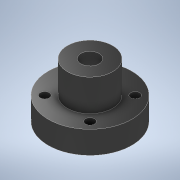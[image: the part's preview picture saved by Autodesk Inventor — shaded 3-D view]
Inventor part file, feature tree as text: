
AUTODESK INVENTOR PART (.ipt)
format: ipt  version: 2022 (Build 260153000, 153)  size: 135,168 bytes
history: native  units: mm
features: extrude x4, sketch x4
ambient origin geometry x8: Origin, YZ Plane, XZ Plane, XY Plane, X Axis, Y Axis, Z Axis, Center Point
bodies: Solid1 (feature_tree)
feature tree (8):
  extrude  "Extrusion1"  Depth=10.0mm
  extrude  "Extrusion2"  Depth=8.0mm
  extrude  "Extrusion3"  Depth=7.0mm
  extrude  "Extrusion4"  Depth=4.0mm TaperAngle=0.0deg
  sketch  "Sketch1"  dims[d0=10.0mm d1=0.0mm d2=20.0mm]
  sketch  "Sketch2"  dims[d3=14.0mm d4=0.0mm d5=8.0mm]
  sketch  "Sketch3"  dims[d6=14.0mm d7=0.0mm d8=7.0mm]
  sketch  "Sketch4"  dims[d9=4.0mm d10=14.0mm d11=0.0mm]
